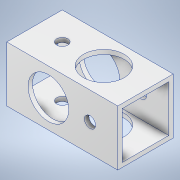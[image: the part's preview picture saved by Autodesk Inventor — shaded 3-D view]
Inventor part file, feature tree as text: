
AUTODESK INVENTOR PART (.ipt)
format: ipt  version: 2020.3 (Build 243373000, 373)  size: 157,184 bytes
history: native  units: mm
features: sketch x5, hole x4, other x1, extrude x1
ambient origin geometry x8: Origin, YZ Plane, XZ Plane, XY Plane, X Axis, Y Axis, Z Axis, Center Point
bodies: Body1 (feature_tree)
feature tree (11):
  other  "ソリッド1"
  extrude  "押し出し1"  Depth=15.0mm
  sketch  "スケッチ2"
  sketch  "スケッチ3"
  hole  "穴1"  [1 undecoded]
  hole  "穴2"  [1 undecoded]
  hole  "穴3"  [1 undecoded]
  hole  "穴4"  [1 undecoded]
  sketch  "スケッチ1"
  sketch  "スケッチ4"
  sketch  "スケッチ5"
note: 4 required parameter values undecoded (feature->parameter linkage not recoverable at this tier; creation-order binding heuristic only, values carry confidence <= 0.55)
